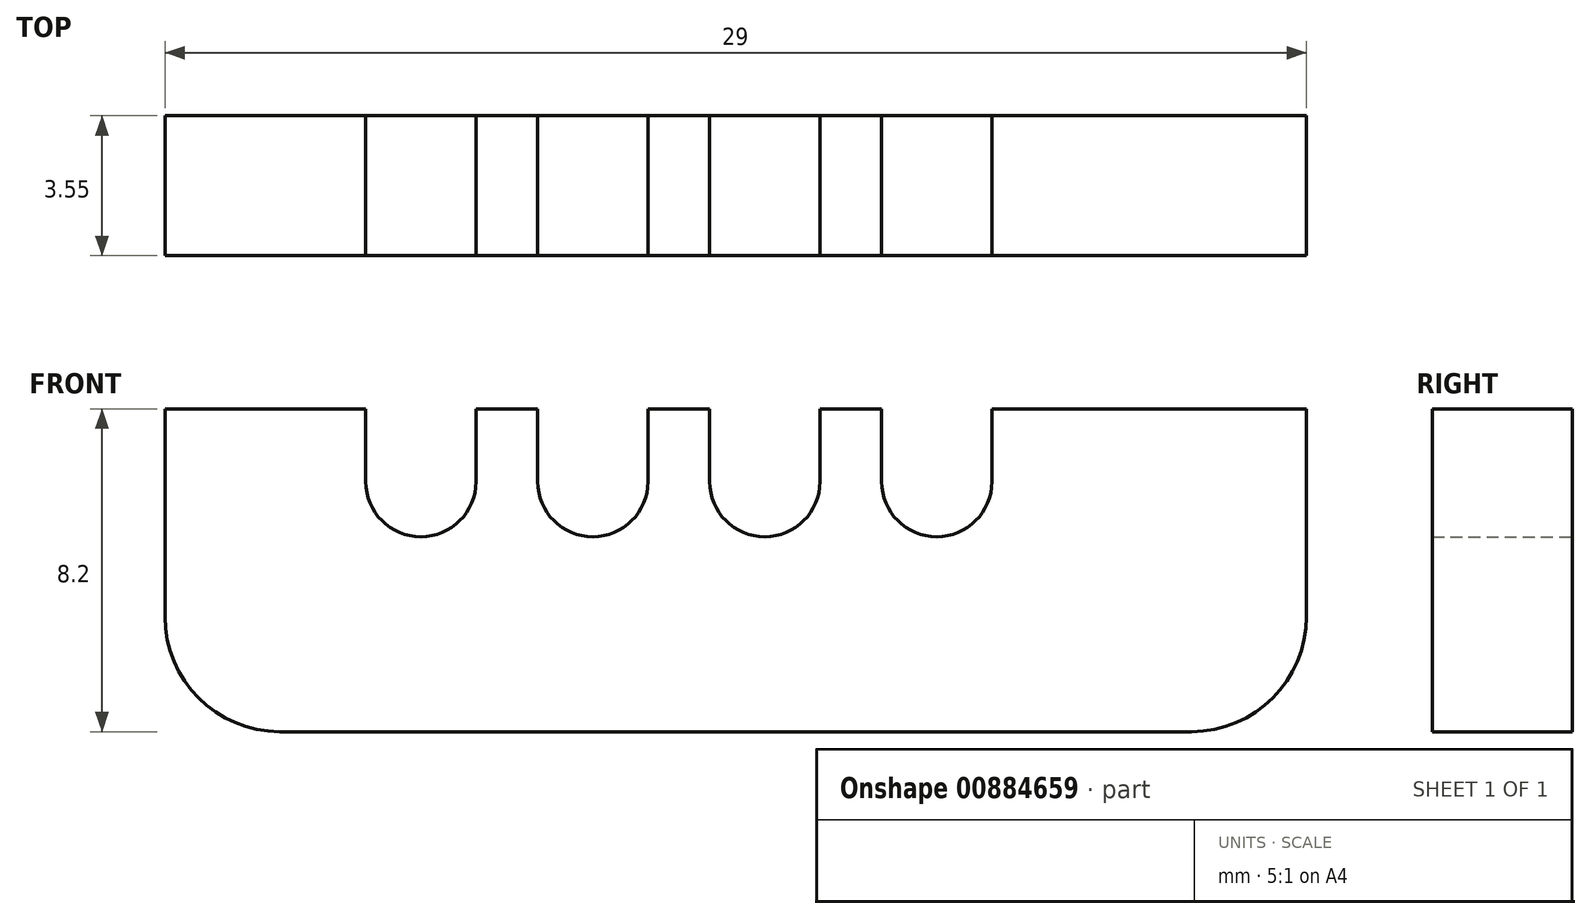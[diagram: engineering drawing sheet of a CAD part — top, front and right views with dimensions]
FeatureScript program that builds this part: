
annotation { "Feature Type Name" : "Feature", "Feature Type Description" : "" }
export const myFeature = defineFeature(function(context is Context, id is Id, definition is map)
    precondition{}
    {
        {
            var Q0;
            Q0=qCreatedBy(makeId("Front.planeOp"),FACE);
            var sketch = newSketch(context, id + "F0", { "sketchPlane" : qUnion([Q0])});
            skArc(sketch, "E0", {"start": v(-105.6, -27.46) * mm, "mid": v(-107.66, -28.32) * mm, "end": v(-108.52, -30.38) * mm});
            skArc(sketch, "E1", {"start": v(-108.52, -48.8) * mm, "mid": v(-107.66, -50.86) * mm, "end": v(-105.6, -51.72) * mm});
            skLineSegment(sketch, "E2", {"start": v(-105.6, -27.46) * mm, "end": v(-79.52, -27.46) * mm});
            skLineSegment(sketch, "E3", {"start": v(-79.52, -51.72) * mm, "end": v(-105.6, -51.72) * mm});
            skLineSegment(sketch, "E4", {"start": v(-108.52, -48.8) * mm, "end": v(-108.52, -30.38) * mm});
            skCircle(sketch, "E5", {"center": v(-99.83, -41.38) * mm, "radius": 1.4 * mm});
            skCircle(sketch, "E6", {"center": v(-95.46, -41.38) * mm, "radius": 1.4 * mm});
            skCircle(sketch, "E7", {"center": v(-91.1, -41.38) * mm, "radius": 1.4 * mm});
            skCircle(sketch, "E8", {"center": v(-86.73, -41.38) * mm, "radius": 1.4 * mm});
            skCircle(sketch, "E9", {"center": v(-102.02, -45.37) * mm, "radius": 1.4 * mm});
            skCircle(sketch, "E10", {"center": v(-97.65, -45.37) * mm, "radius": 1.4 * mm});
            skCircle(sketch, "E11", {"center": v(-93.28, -45.37) * mm, "radius": 1.4 * mm});
            skCircle(sketch, "E12", {"center": v(-88.91, -45.37) * mm, "radius": 1.4 * mm});
            skCircle(sketch, "E13", {"center": v(-76.58, -39.6) * mm, "radius": 1.6 * mm});
            skCircle(sketch, "E14", {"center": v(-76.58, -31.97) * mm, "radius": 1.2 * mm});
            skCircle(sketch, "E15", {"center": v(-76.58, -46.7) * mm, "radius": 1.2 * mm});
            skCircle(sketch, "E16", {"center": v(-76.58, -47.72) * mm, "radius": 1.2 * mm});
            skLineSegment(sketch, "E17", {"start": v(-79.52, -43.22) * mm, "end": v(-79.52, -51.72) * mm});
            skArc(sketch, "E18", {"start": v(-82.44, -51.72) * mm, "mid": v(-80.38, -50.86) * mm, "end": v(-79.52, -48.8) * mm});
            skLineSegment(sketch, "E19", {"start": v(-108.52, -43.52) * mm, "end": v(-74.05, -43.52) * mm});
            skLineSegment(sketch, "E20", {"start": v(-108.52, -43.23) * mm, "end": v(-74.04, -43.23) * mm});
            skLineSegment(sketch, "E21", {"start": v(-79.52, -43.22) * mm, "end": v(-79.52, -27.46) * mm});
            skArc(sketch, "E22", {"start": v(-79.52, -30.38) * mm, "mid": v(-80.38, -28.32) * mm, "end": v(-82.44, -27.46) * mm});
            skLineSegment(sketch, "E23", {"start": v(-110.85, -55.44) * mm, "end": v(-77.56, -55.44) * mm, "construction": true});
            skLineSegment(sketch, "E24.bottom", {"start": v(-103.42, -45.37) * mm, "end": v(-100.62, -45.37) * mm});
            skLineSegment(sketch, "E24.top", {"start": v(-103.42, -43.52) * mm, "end": v(-100.62, -43.52) * mm});
            skLineSegment(sketch, "E24.left", {"start": v(-103.42, -45.37) * mm, "end": v(-103.42, -43.52) * mm});
            skLineSegment(sketch, "E24.right", {"start": v(-100.62, -45.37) * mm, "end": v(-100.62, -43.52) * mm});
            skLineSegment(sketch, "E25.bottom", {"start": v(-99.05, -43.52) * mm, "end": v(-96.25, -43.52) * mm});
            skLineSegment(sketch, "E25.top", {"start": v(-99.05, -45.37) * mm, "end": v(-96.25, -45.37) * mm});
            skLineSegment(sketch, "E25.left", {"start": v(-99.05, -43.52) * mm, "end": v(-99.05, -45.37) * mm});
            skLineSegment(sketch, "E25.right", {"start": v(-96.25, -43.52) * mm, "end": v(-96.25, -45.37) * mm});
            skLineSegment(sketch, "E26.bottom", {"start": v(-94.68, -43.52) * mm, "end": v(-91.88, -43.52) * mm});
            skLineSegment(sketch, "E26.top", {"start": v(-94.68, -45.37) * mm, "end": v(-91.88, -45.37) * mm});
            skLineSegment(sketch, "E26.left", {"start": v(-94.68, -43.52) * mm, "end": v(-94.68, -45.37) * mm});
            skLineSegment(sketch, "E26.right", {"start": v(-91.88, -43.52) * mm, "end": v(-91.88, -45.37) * mm});
            skLineSegment(sketch, "E27.bottom", {"start": v(-90.31, -43.52) * mm, "end": v(-87.51, -43.52) * mm});
            skLineSegment(sketch, "E27.top", {"start": v(-90.31, -45.37) * mm, "end": v(-87.51, -45.37) * mm});
            skLineSegment(sketch, "E27.left", {"start": v(-90.31, -43.52) * mm, "end": v(-90.31, -45.37) * mm});
            skLineSegment(sketch, "E27.right", {"start": v(-87.51, -43.52) * mm, "end": v(-87.51, -45.37) * mm});
            skLineSegment(sketch, "E28.bottom", {"start": v(-101.23, -41.38) * mm, "end": v(-98.43, -41.38) * mm});
            skLineSegment(sketch, "E28.top", {"start": v(-101.23, -43.23) * mm, "end": v(-98.43, -43.23) * mm});
            skLineSegment(sketch, "E28.left", {"start": v(-101.23, -41.38) * mm, "end": v(-101.23, -43.23) * mm});
            skLineSegment(sketch, "E28.right", {"start": v(-98.43, -41.38) * mm, "end": v(-98.43, -43.23) * mm});
            skLineSegment(sketch, "E29.bottom", {"start": v(-96.86, -41.38) * mm, "end": v(-94.06, -41.38) * mm});
            skLineSegment(sketch, "E29.top", {"start": v(-96.86, -43.23) * mm, "end": v(-94.06, -43.23) * mm});
            skLineSegment(sketch, "E29.left", {"start": v(-96.86, -41.38) * mm, "end": v(-96.86, -43.23) * mm});
            skLineSegment(sketch, "E29.right", {"start": v(-94.06, -41.38) * mm, "end": v(-94.06, -43.23) * mm});
            skLineSegment(sketch, "E30.bottom", {"start": v(-92.5, -41.38) * mm, "end": v(-89.7, -41.38) * mm});
            skLineSegment(sketch, "E30.top", {"start": v(-92.5, -43.23) * mm, "end": v(-89.7, -43.23) * mm});
            skLineSegment(sketch, "E30.left", {"start": v(-92.5, -41.38) * mm, "end": v(-92.5, -43.23) * mm});
            skLineSegment(sketch, "E30.right", {"start": v(-89.7, -41.38) * mm, "end": v(-89.7, -43.23) * mm});
            skLineSegment(sketch, "E31.bottom", {"start": v(-88.13, -41.38) * mm, "end": v(-85.33, -41.38) * mm});
            skLineSegment(sketch, "E31.top", {"start": v(-88.13, -43.23) * mm, "end": v(-85.33, -43.23) * mm});
            skLineSegment(sketch, "E31.left", {"start": v(-88.13, -41.38) * mm, "end": v(-88.13, -43.23) * mm});
            skLineSegment(sketch, "E31.right", {"start": v(-85.33, -41.38) * mm, "end": v(-85.33, -43.23) * mm});
            skSolve(sketch);
        }
        {
            var Q0;
            {var subQ15=sQuery(id+"F0.wireOp",EDGE,"E1");Q0=makeQuery(id+"F0.imprint","IMPRINT",FACE,{"disambiguationData":[TD([[makeQuery(id+"F0.imprint","IMPRINT",EDGE,{"derivedFrom":subQ15}),1.0]])]});}
            extrude(context, id + "F1", {"entities" : qUnion([Q0]), "depth" : 3.55 * mm, "offsetDistance" : 25 * mm});
        }
    });
